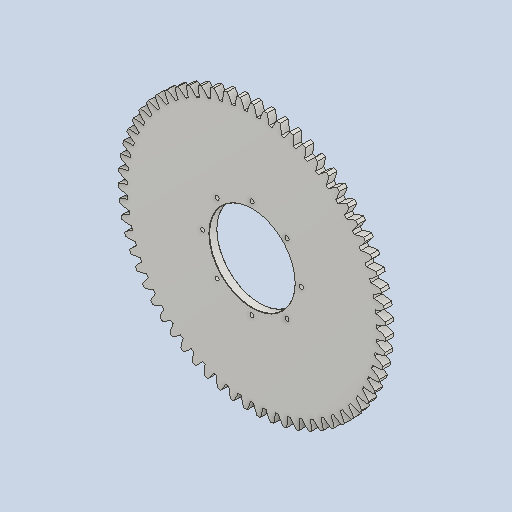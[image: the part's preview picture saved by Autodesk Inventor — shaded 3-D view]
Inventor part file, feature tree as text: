
AUTODESK INVENTOR PART (.ipt)
format: ipt  version: 2024.2 (Build 282272000, 272)  size: 579,072 bytes
history: native  units: mm (DEFAULTED — no unit token found)
features: extrude x3, plane x3, other x3, sketch x3, pattern_circular x1, fillet x1, projected_geometry x1
ambient origin geometry x8: Origin, YZ Plane, XZ Plane, XY Plane, X Axis, Y Axis, Z Axis, Center Point
bodies: Solid1 (feature_tree)
feature tree (15):
  extrude  "Extrusion1"  Depth=24.0mm TaperAngle=0.0deg
  plane  "Work Plane2"
  plane  "Work Plane8"
  plane  "Work Plane9"
  other  "Spur Gear"
  extrude  "Extrusion2"  Depth=10.0mm TaperAngle=0.0deg
  extrude  "Extrusion3"  Depth=1.0mm TaperAngle=0.0deg
  pattern_circular  "Circular Pattern1"  [2 undecoded]
  fillet  "Fillet1"  [1 undecoded]
  sketch  "Sketch1"  dims[d0=812.91152mm d1=24.0mm d2=0.0mm]
  other  "Srf1"
  sketch  "Sketch3"  dims[d3=787.89816mm d4=10.0mm d5=0.0mm]
  projected_geometry  "Projected Loop1"
  sketch  "Sketch4"  dims[d16=494.0mm d17=0.0mm d34=0.498666mm d39=0.0mm d41=0.0mm d43=494.0mm d46=494.0mm d47=0.0mm d48=0.0mm d49=260.0mm d50=0.0mm d51=0.0mm d52=12.5mm d53=150.0mm d54=0.0mm d55=0.0mm d56=80.0mm d57=360.0deg d59=1.0mm]
  other  "Pitch Diameter"
note: 3 required parameter values undecoded (feature->parameter linkage not recoverable at this tier; creation-order binding heuristic only, values carry confidence <= 0.55)
